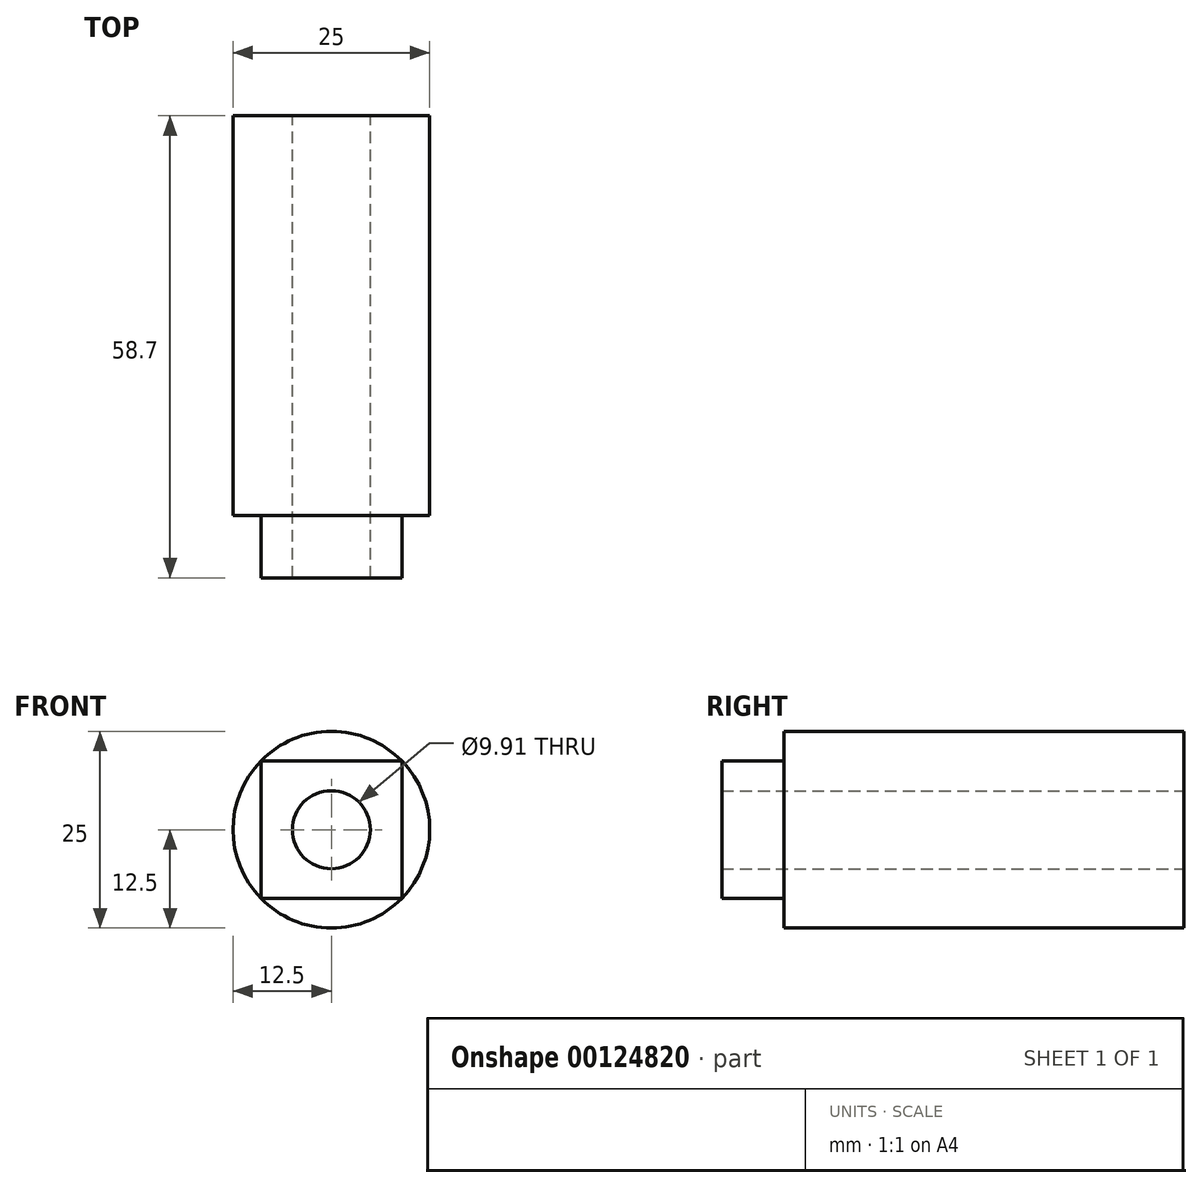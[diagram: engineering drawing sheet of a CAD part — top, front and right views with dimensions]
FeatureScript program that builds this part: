
annotation { "Feature Type Name" : "Feature", "Feature Type Description" : "" }
export const myFeature = defineFeature(function(context is Context, id is Id, definition is map)
    precondition{}
    {
        {
            var Q0;
            Q0=qCreatedBy(makeId("Front.planeOp"),FACE);
            var sketch = newSketch(context, id + "F0", { "sketchPlane" : qUnion([Q0])});
            skCircle(sketch, "E0", {"center": v(0, 0) * mm, "radius": 12.5 * mm});
            skCircle(sketch, "E1", {"center": v(0, 0) * mm, "radius": 4.95 * mm});
            skLineSegment(sketch, "E2.bottom", {"start": v(8.95, -8.72) * mm, "end": v(-8.95, -8.72) * mm});
            skLineSegment(sketch, "E2.top", {"start": v(8.95, 8.72) * mm, "end": v(-8.95, 8.72) * mm});
            skLineSegment(sketch, "E2.left", {"start": v(8.95, -8.72) * mm, "end": v(8.95, 8.72) * mm});
            skLineSegment(sketch, "E2.right", {"start": v(-8.95, -8.72) * mm, "end": v(-8.95, 8.72) * mm});
            skSolve(sketch);
        }
        {
            var Q0;
            Q0=makeQuery(id+"F0.imprint","IMPRINT",FACE,{"disambiguationData":[TD([[makeQuery(id+"F0.imprint","IMPRINT",EDGE,{"derivedFrom":sQuery(id+"F0.wireOp",EDGE,"E1")}),-1.0]])]});
            extrude(context, id + "F1", {"entities" : qUnion([Q0]), "depth" : 7.9 * mm});
        }
        {
            var Q0;
            Q0=qCreatedBy(makeId("Front.planeOp"),FACE);
            var sketch = newSketch(context, id + "F2", { "sketchPlane" : qUnion([Q0])});
            skCircle(sketch, "E3", {"center": v(0, 0) * mm, "radius": 12.5 * mm});
            skSolve(sketch);
        }
        {
            var Q0;
            Q0=makeQuery(id+"F2.imprint","IMPRINT",FACE,{"disambiguationData":[TD([[makeQuery(id+"F2.imprint","IMPRINT",EDGE,{"derivedFrom":sQuery(id+"F2.wireOp",EDGE,"E3")}),1.0]])]});
            extrude(context, id + "F3", {"entities" : qUnion([Q0]), "operationType" : NewBodyOperationType.ADD, "oppositeDirection" : true, "depth" : 50.8 * mm});
        }
        {
            var Q0;
            Q0=makeQuery(id+"F3.boolean.opBoolean","SPLIT",FACE,{"disambiguationData":[TD([makeQuery(id+"F1.opExtrude","SWEPT_FACE",FACE,{"disambiguationData":[OSD([sQuery(id+"F0.wireOp",EDGE,"E1")])]})])],"derivedFrom":makeQuery(id+"F3.opExtrude","CAP_FACE",FACE,{"disambiguationData":[OSD([sQuery(id+"F2.wireOp",EDGE,"E3")])],"isStart":true})});
            extrude(context, id + "F4", {"entities" : qUnion([Q0]), "operationType" : NewBodyOperationType.REMOVE, "oppositeDirection" : true, "depth" : 50.8 * mm});
        }
    });
